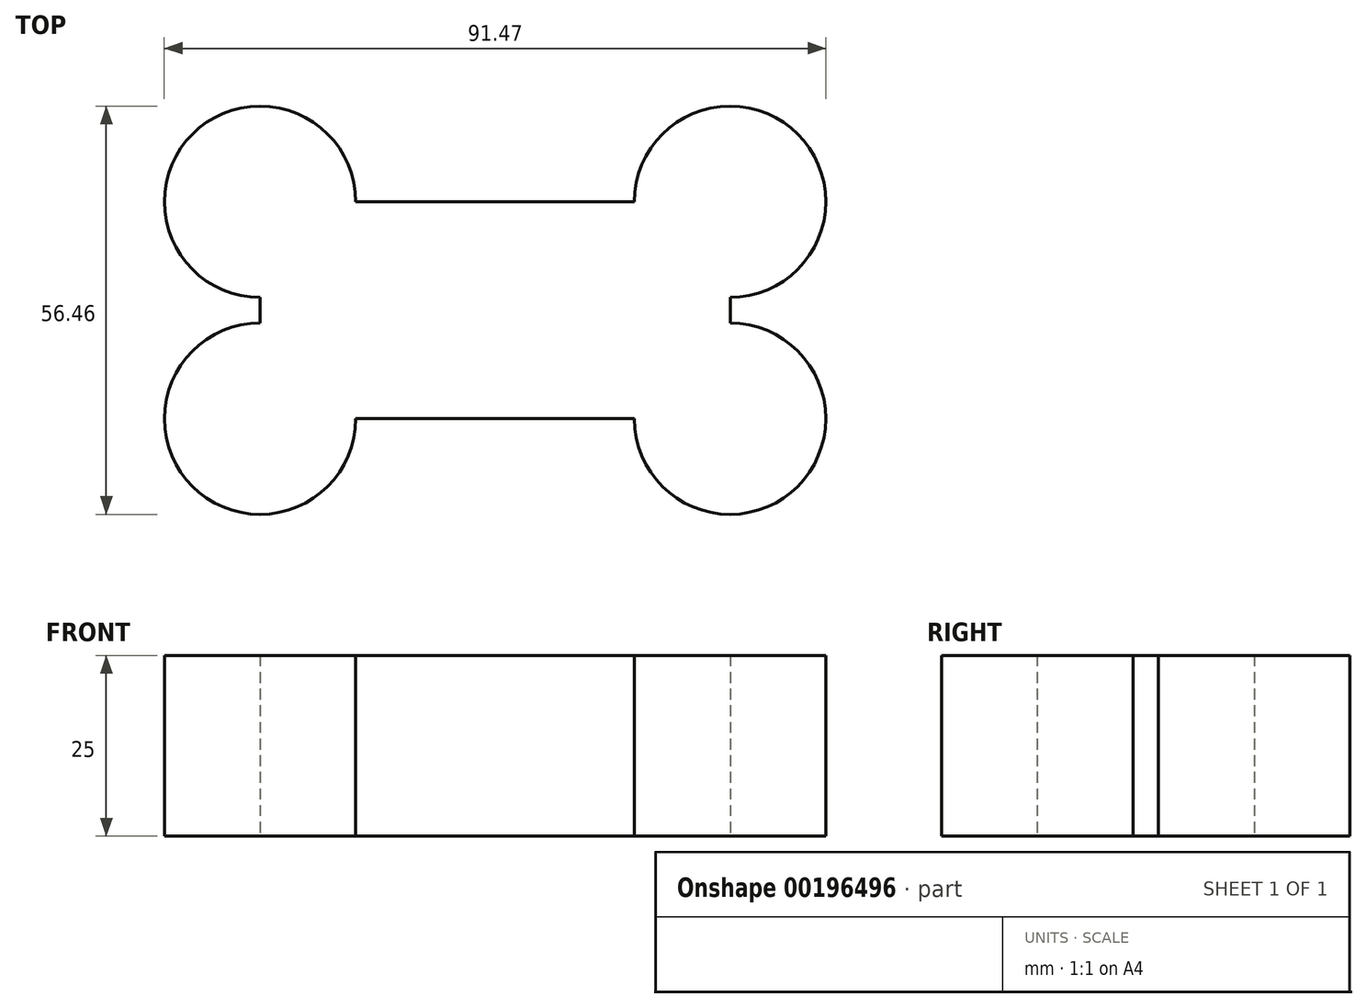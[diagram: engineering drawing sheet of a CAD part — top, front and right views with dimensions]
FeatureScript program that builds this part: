
annotation { "Feature Type Name" : "Feature", "Feature Type Description" : "" }
export const myFeature = defineFeature(function(context is Context, id is Id, definition is map)
    precondition{}
    {
        {
            var Q0;
            Q0=qCreatedBy(makeId("Top.planeOp"),FACE);
            var sketch = newSketch(context, id + "F0", { "sketchPlane" : qUnion([Q0])});
            skLineSegment(sketch, "E0.bottom", {"start": v(-23.57, 8.72) * mm, "end": v(14.96, 8.72) * mm});
            skLineSegment(sketch, "E0.top", {"start": v(-23.57, -21.28) * mm, "end": v(14.96, -21.28) * mm});
            skLineSegment(sketch, "E0.left", {"start": v(-36.8, -4.51) * mm, "end": v(-36.8, -8.05) * mm});
            skLineSegment(sketch, "E0.right", {"start": v(28.2, -4.51) * mm, "end": v(28.2, -8.05) * mm});
            skArc(sketch, "E1", {"start": v(-23.57, 8.72) * mm, "mid": v(-46.16, 18.08) * mm, "end": v(-36.8, -4.51) * mm});
            skArc(sketch, "E2", {"start": v(-36.8, -8.05) * mm, "mid": v(-46.16, -30.64) * mm, "end": v(-23.57, -21.28) * mm});
            skArc(sketch, "E3", {"start": v(28.2, -4.51) * mm, "mid": v(37.55, 18.08) * mm, "end": v(14.96, 8.72) * mm});
            skArc(sketch, "E4", {"start": v(14.96, -21.28) * mm, "mid": v(37.55, -30.64) * mm, "end": v(28.2, -8.05) * mm});
            skSolve(sketch);
        }
        {
            var Q0;
            Q0=makeQuery(id+"F0.imprint","IMPRINT",FACE,{"disambiguationData":[TD([[makeQuery(id+"F0.imprint","IMPRINT",EDGE,{"derivedFrom":sQuery(id+"F0.wireOp",EDGE,"E0.bottom")}),-1.0]])]});
            extrude(context, id + "F1", {"entities" : qUnion([Q0]), "depth" : 25 * mm});
        }
    });
